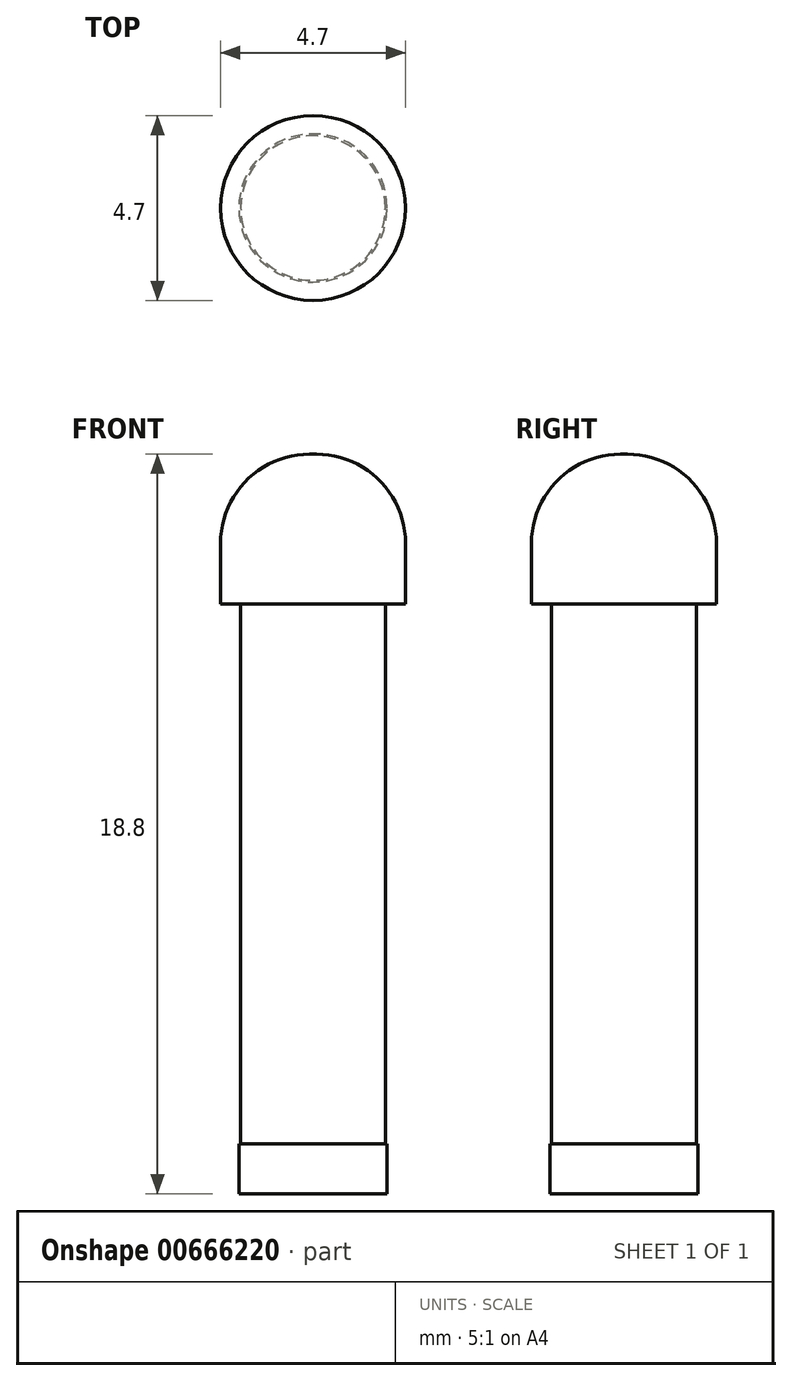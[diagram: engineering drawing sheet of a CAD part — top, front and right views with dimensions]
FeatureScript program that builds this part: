
annotation { "Feature Type Name" : "Feature", "Feature Type Description" : "" }
export const myFeature = defineFeature(function(context is Context, id is Id, definition is map)
    precondition{}
    {
        {
            var Q0;
            Q0=qCreatedBy(makeId("Top.planeOp"),FACE);
            var sketch = newSketch(context, id + "F0", { "sketchPlane" : qUnion([Q0])});
            skCircle(sketch, "E0", {"center": v(0, 0) * mm, "radius": 1.84 * mm});
            skSolve(sketch);
        }
        {
            var Q0;
            Q0=makeQuery(id+"F0.imprint","IMPRINT",FACE,{"disambiguationData":[TD([[makeQuery(id+"F0.imprint","IMPRINT",EDGE,{"derivedFrom":sQuery(id+"F0.wireOp",EDGE,"E0")}),1.0]])]});
            extrude(context, id + "F1", {"entities" : qUnion([Q0]), "depth" : 13.72 * mm, "offsetDistance" : 25.4 * mm});
        }
        {
            var Q0;
            Q0=makeQuery(id+"F1.opExtrude","CAP_FACE",FACE,{"disambiguationData":[OSD([sQuery(id+"F0.wireOp",EDGE,"E0")])],"isStart":false});
            var sketch = newSketch(context, id + "F2", { "sketchPlane" : qUnion([Q0])});
            skCircle(sketch, "E1", {"center": v(0, 0) * mm, "radius": 2.35 * mm});
            skSolve(sketch);
        }
        {
            var Q0;
            Q0 = qSketchRegion(id + "F2", true);
            extrude(context, id + "F3", {"entities" : qUnion([Q0]), "depth" : 3.8 * mm, "offsetDistance" : 25.4 * mm});
        }
        {
            var Q0;
            Q0=makeQuery(id+"F3.opExtrude","CAP_FACE",FACE,{"disambiguationData":[OSD([sQuery(id+"F2.wireOp",EDGE,"E1")])],"isStart":false});
            fillet(context, id + "F4", {"entities" : qUnion([Q0]), "radius" : 2.26 * mm, "tangentPropagation" : true, "allowEdgeOverflow" : false});
        }
        {
            var Q0;
            Q0=makeQuery(id+"F1.opExtrude","CAP_FACE",FACE,{"disambiguationData":[OSD([sQuery(id+"F0.wireOp",EDGE,"E0")])],"isStart":true});
            var sketch = newSketch(context, id + "F5", { "sketchPlane" : qUnion([Q0])});
            skCircle(sketch, "E2", {"center": v(0, 0) * mm, "radius": 1.88 * mm});
            skSolve(sketch);
        }
        {
            var Q0;
            Q0=makeQuery(id+"F5.imprint","IMPRINT",FACE,{"disambiguationData":[TD([[makeQuery(id+"F5.imprint","IMPRINT",EDGE,{"derivedFrom":makeQuery(id+"F1.opExtrude","CAP_EDGE",EDGE,{"disambiguationData":[OSD([sQuery(id+"F0.wireOp",EDGE,"E0")])],"isStart":true})}),-1.0]])]});
            var Q1;
            Q1=makeQuery(id+"F5.imprint","IMPRINT",FACE,{"disambiguationData":[TD([[makeQuery(id+"F5.imprint","IMPRINT",EDGE,{"derivedFrom":sQuery(id+"F5.wireOp",EDGE,"E2")}),1.0]])]});
            extrude(context, id + "F6", {"entities" : qUnion([Q0, Q1]), "depth" : 1.27 * mm, "offsetDistance" : 25.4 * mm});
        }
    });
